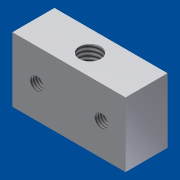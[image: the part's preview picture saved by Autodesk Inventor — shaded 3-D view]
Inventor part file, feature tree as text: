
AUTODESK INVENTOR PART (.ipt)
format: ipt  version: 2013 (Build 170138000, 138)  size: 103,424 bytes
history: native  units: in
note: dims shown in document units (in); Inventor stores cm internally (conversion verified against a paired STEP export)
features: sketch x3, hole x2, extrude x1
ambient origin geometry x8: Origin, YZ Plane, XZ Plane, XY Plane, X Axis, Y Axis, Z Axis, Center Point
bodies: Solid1 (feature_tree)
feature tree (6):
  extrude  "Extrusion1"  Depth=0.7874in
  hole  "Hole1"  [1 undecoded]
  hole  "Hole2"  [1 undecoded]
  sketch  "Sketch1"  dims[d0=1.378in d1=0.7874in]
  sketch  "Sketch2"  dims[d2=0.3937in d3=0.689in]
  sketch  "Sketch3"  dims[d4=0.5118in d5=0.0in d6=0.1654in d7=0.1654in d8=0.7874in d9=0.3937in d10=0.3937in d11=0.2953in d12=0.1628in d13=0.2362in d14=0.1575in d15=0.0787in d16=90.0deg d17=0.315in d18=0.8108in d19=0.2657in d20=0.689in d21=0.2559in d22=0.2617in d23=0.2362in d24=0.1575in d25=0.0787in d26=90.0deg d27=0.315in d28=0.8108in]
note: 2 required parameter values undecoded (feature->parameter linkage not recoverable at this tier; creation-order binding heuristic only, values carry confidence <= 0.55)
